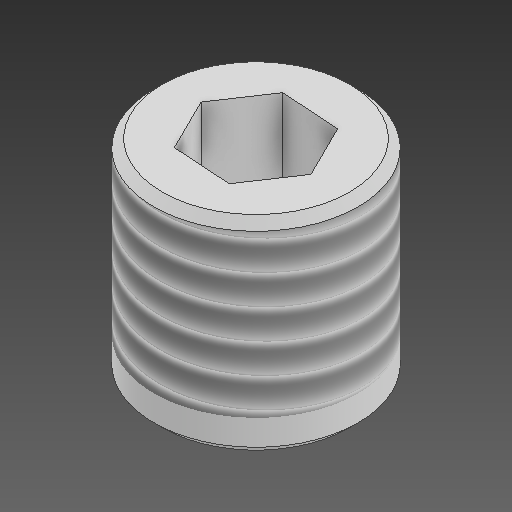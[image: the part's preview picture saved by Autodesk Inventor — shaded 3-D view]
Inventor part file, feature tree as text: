
AUTODESK INVENTOR PART (.ipt)
format: ipt  version: 2021 (Build 250183000, 183)  size: 174,080 bytes
history: native  units: in
note: dims shown in document units (in); Inventor stores cm internally (conversion verified against a paired STEP export)
features: other x3, sketch x2
ambient origin geometry x8: Origin, YZ Plane, XZ Plane, XY Plane, X Axis, Y Axis, Z Axis, Center Point
bodies: Solid1 (feature_tree)
feature tree (5):
  other  "M12_HEX.ipt"
  other  "Solid1::M12_HEX.ipt"
  other  "TaggingFeature1"
  sketch  "Sketch1"  dims[d0=0.3937in]
  sketch  "Sketch2"
